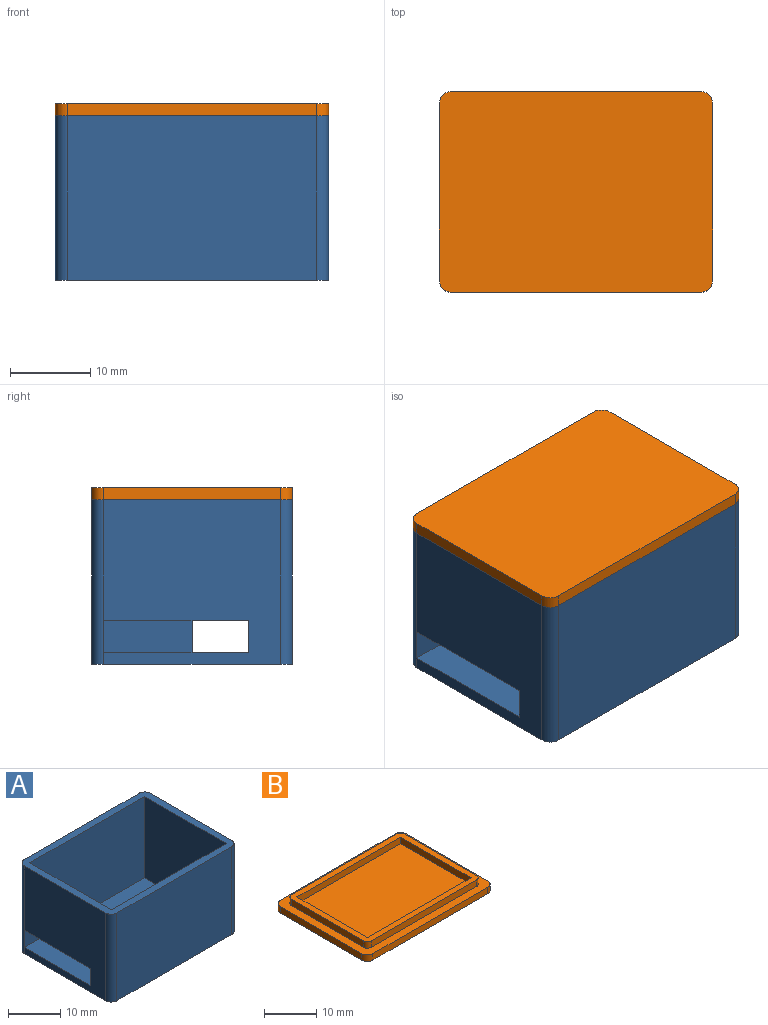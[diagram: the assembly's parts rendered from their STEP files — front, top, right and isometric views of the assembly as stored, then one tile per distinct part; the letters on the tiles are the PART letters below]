
ASSEMBLY  parts=2 mates=1
PART A: 19 faces, bbox 34x25x20.5 mm
  f0: plane 22x20.5mm, normal (-1,0,0), area 379mm2, adj f8,f9,f10,f13,f14,f17,f18
  f1: plane 22x20.5mm, normal (1,0,0), area 407mm2, adj f8,f9,f10,f11,f12,f15,f16
  f2: plane 31x20.5mm, normal (0,-1,0), area 635.5mm2, adj f8,f9,f11,f14
  f3: plane 31x20.5mm, normal (0,1,0), area 635.5mm2, adj f8,f9,f12,f13
  f4: plane 22x19mm, normal (-1,0,0), area 374mm2, adj f5,f7,f8,f10,f15,f16
  f5: plane 32.5x19mm, normal (0,1,0), area 595mm2, adj f4,f6,f8,f10,f11,f16
  f6: plane 22x19mm, normal (1,0,0), area 346mm2, adj f5,f7,f8,f10,f17,f18
  f7: plane 32.5x19mm, normal (0,-1,0), area 595mm2, adj f4,f6,f8,f10,f13,f18
  f8: plane 34x25mm, normal (0,0,1), area 166.1mm2, adj f0,f1,f2,f3,f4,f5,f6,f7
  f9: plane 34x25mm, normal (0,0,-1), area 848.1mm2, adj f0,f1,f2,f3,f11,f12,f13,f14
  f10: plane 34x22mm, normal (0,0,1), area 725.5mm2, adj f0,f1,f4,f5,f6,f7,f15,f17
  f11: cylinder r=1.5mm len=20.5mm, axis (0,0,1), area 48.3mm2, adj f1,f2,f5,f8,f9
  f12: cylinder r=1.5mm len=20.5mm, axis (0,0,-1), area 48.3mm2, adj f1,f3,f8,f9
  f13: cylinder r=1.5mm len=20.5mm, axis (0,0,1), area 48.3mm2, adj f0,f3,f7,f8,f9
  f14: cylinder r=1.5mm len=20.5mm, axis (0,0,-1), area 48.3mm2, adj f0,f2,f8,f9
  f15: plane 4x1.5mm, normal (0,-1,0), area 6mm2, adj f1,f4,f10,f16
  f16: plane 11x1.5mm, normal (0,0,-1), area 16.5mm2, adj f1,f4,f5,f15
  f17: plane 4x1.5mm, normal (0,1,0), area 6mm2, adj f0,f6,f10,f18
  f18: plane 18x1.5mm, normal (0,0,-1), area 27mm2, adj f0,f6,f7,f17
PART B: 24 faces, bbox 34x25x3 mm
  f0: plane 34x25mm, normal (0,0,1), area 193.2mm2, adj f1,f2,f3,f4,f6,f7,f8,f13
  f1: plane 31x1.5mm, normal (0,-1,0), area 46.5mm2, adj f0,f5,f16,f19
  f2: plane 22x1.5mm, normal (1,0,0), area 33mm2, adj f0,f5,f16,f17
  f3: plane 31x1.5mm, normal (0,1,0), area 46.5mm2, adj f0,f5,f17,f18
  f4: plane 22x1.5mm, normal (-1,0,0), area 33mm2, adj f0,f5,f18,f19
  f5: plane 34x25mm, normal (0,0,-1), area 848.1mm2, adj f1,f2,f3,f4,f16,f17,f18,f19
  f6: plane 28.5x1.5mm, normal (0,-1,0), area 42.7mm2, adj f0,f14,f20,f23
  f7: plane 19.5x1.5mm, normal (1,0,0), area 29.2mm2, adj f0,f14,f20,f21
  f8: plane 28.5x1.5mm, normal (0,1,0), area 42.7mm2, adj f0,f14,f21,f22
  f9: plane 19x1.5mm, normal (-1,0,0), area 28.5mm2, adj f10,f12,f14,f15
  f10: plane 28x1.5mm, normal (0,1,0), area 42mm2, adj f9,f11,f14,f15
  f11: plane 19x1.5mm, normal (1,0,0), area 28.5mm2, adj f10,f12,f14,f15
  f12: plane 28x1.5mm, normal (0,-1,0), area 42mm2, adj f9,f11,f14,f15
  f13: plane 19.5x1.5mm, normal (-1,0,0), area 29.2mm2, adj f0,f14,f22,f23
  f14: plane 30.5x21.5mm, normal (0,0,1), area 122.9mm2, adj f6,f7,f8,f9,f10,f11,f12,f13
  f15: plane 28x19mm, normal (0,0,1), area 532mm2, adj f9,f10,f11,f12
  f16: cylinder r=1.5mm len=1.5mm, axis (0,0,-1), area 3.5mm2, adj f0,f1,f2,f5
  f17: cylinder r=1.5mm len=1.5mm, axis (0,0,1), area 3.5mm2, adj f0,f2,f3,f5
  f18: cylinder r=1.5mm len=1.5mm, axis (0,0,-1), area 3.5mm2, adj f0,f3,f4,f5
  f19: cylinder r=1.5mm len=1.5mm, axis (0,0,1), area 3.5mm2, adj f0,f1,f4,f5
  f20: cylinder r=1mm len=1.5mm, axis (0,0,1), area 2.4mm2, adj f0,f6,f7,f14
  f21: cylinder r=1mm len=1.5mm, axis (0,0,-1), area 2.4mm2, adj f0,f7,f8,f14
  f22: cylinder r=1mm len=1.5mm, axis (0,0,1), area 2.4mm2, adj f0,f8,f13,f14
  f23: cylinder r=1mm len=1.5mm, axis (0,0,-1), area 2.4mm2, adj f0,f6,f13,f14
PLACE A t=(-3.47,3.66,-1.76)mm
PLACE B rot(axis=(1,0,0),180deg) t=(-3.47,3.66,18.74)mm
MATE fastened B.f19 <-> A.f13  axis (0,0,-1) through (-18.97,14.66,18.74)mm
